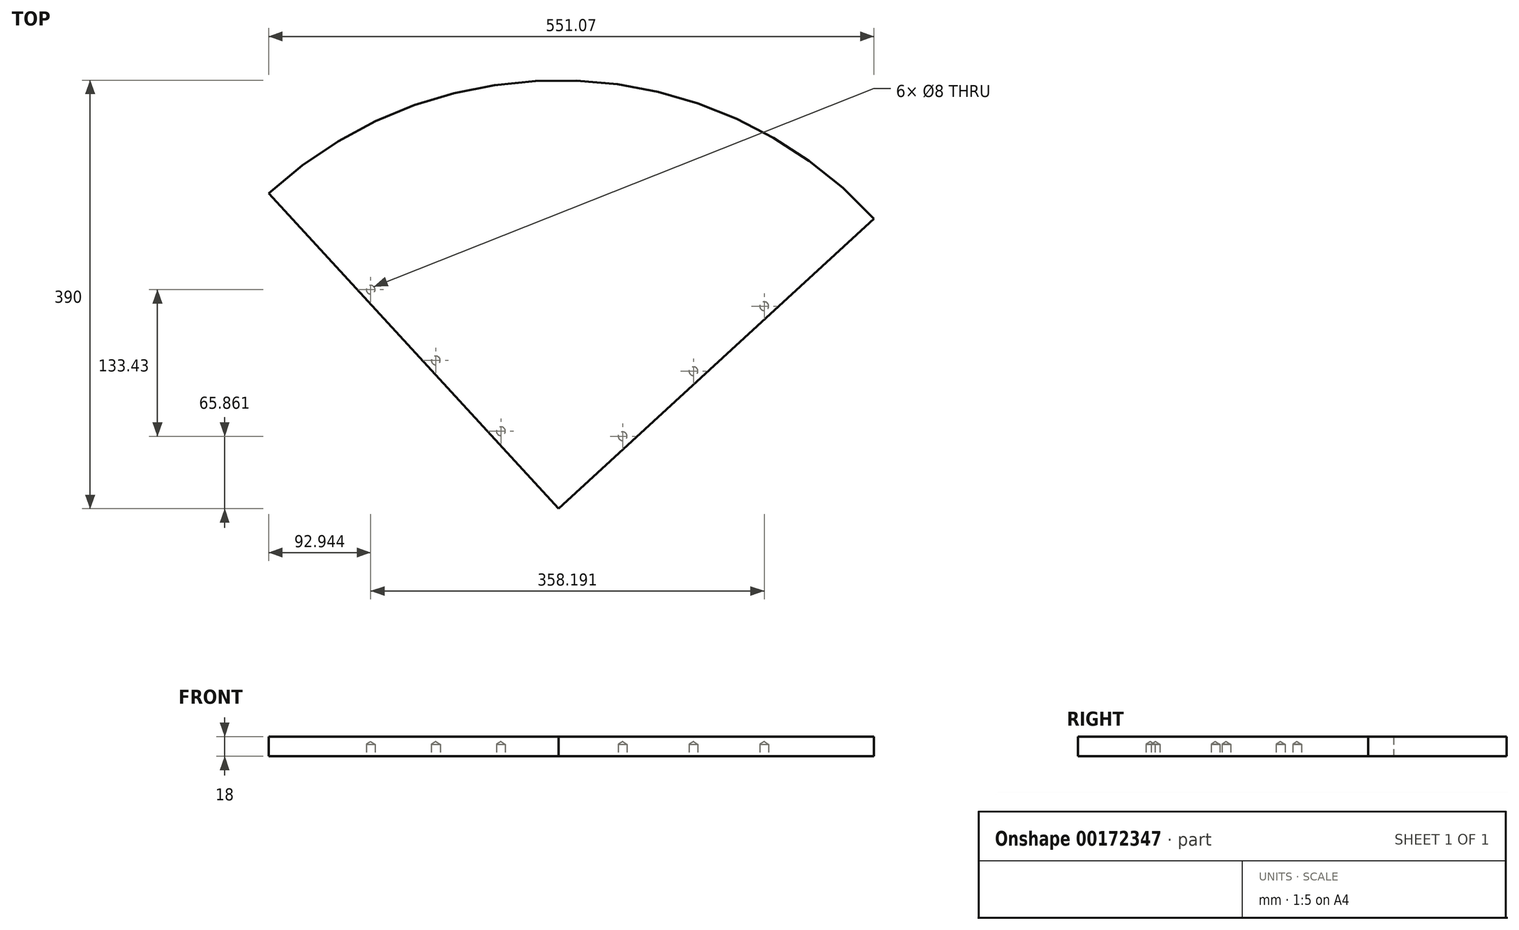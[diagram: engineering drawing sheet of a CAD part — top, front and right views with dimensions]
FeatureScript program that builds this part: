
annotation { "Feature Type Name" : "Feature", "Feature Type Description" : "" }
export const myFeature = defineFeature(function(context is Context, id is Id, definition is map)
    precondition{}
    {
        {
            var Q0;
            Q0=qCreatedBy(makeId("Top.planeOp"),FACE);
            var sketch = newSketch(context, id + "F0", { "sketchPlane" : qUnion([Q0])});
            skArc(sketch, "E0", {"start": v(-264.03, 287.04) * mm, "mid": v(16.27, 389.66) * mm, "end": v(287.04, 264.03) * mm});
            skLineSegment(sketch, "E1", {"start": v(-264.03, 287.04) * mm, "end": v(0, 0) * mm});
            skLineSegment(sketch, "E2", {"start": v(287.04, 264.03) * mm, "end": v(0, 0) * mm});
            skSolve(sketch);
        }
        {
            var Q0;
            {var subQ0=sQuery(id+"F0.wireOp",EDGE,"qqqJjdmg-fhSf-ph05-KDBg-snlAx8Mx0EB6");Q0=makeQuery(id+"F0.imprint","IMPRINT",FACE,{"disambiguationData":[TD([[makeQuery(id+"F0.imprint","IMPRINT",EDGE,{"derivedFrom":subQ0}),1.0]])]});}
            var Q1;
            {var subQ0=sQuery(id+"F0.wireOp",EDGE,"E1");Q1=makeQuery(id+"F0.imprint","IMPRINT",FACE,{"disambiguationData":[TD([[makeQuery(id+"F0.imprint","IMPRINT",EDGE,{"derivedFrom":subQ0}),1.0]])]});}
            var Q2;
            {var subQ0=sQuery(id+"F0.wireOp",EDGE,"E2");Q2=makeQuery(id+"F0.imprint","IMPRINT",FACE,{"disambiguationData":[TD([[makeQuery(id+"F0.imprint","IMPRINT",EDGE,{"derivedFrom":subQ0}),-1.0]])]});}
            extrude(context, id + "F1", {"entities" : qUnion([Q0, Q1, Q2]), "depth" : 18 * mm});
        }
        {
            var Q0;
            Q0=makeQuery(id+"F1.opExtrude","CAP_FACE",FACE,{"disambiguationData":[OSD([sQuery(id+"F0.wireOp",EDGE,"E0"),sQuery(id+"F0.wireOp",EDGE,"E1"),sQuery(id+"F0.wireOp",EDGE,"E2")])],"isStart":true});
            var sketch = newSketch(context, id + "F2", { "sketchPlane" : qUnion([Q0])});
            skPoint(sketch, "E3", {"position": v(-52.61, -70.5) * mm});
            skPoint(sketch, "E4", {"position": v(-111.85, -134.9) * mm});
            skPoint(sketch, "E5", {"position": v(-171.09, -199.3) * mm});
            skPoint(sketch, "E6", {"position": v(58.3, -65.86) * mm});
            skPoint(sketch, "E7", {"position": v(122.7, -125.1) * mm});
            skPoint(sketch, "E8", {"position": v(187.1, -184.33) * mm});
            skSolve(sketch);
        }
        {
            var Q0;
            Q0=sQuery(id+"F2.wireOp",VERTEX,"E4");
            var Q1;
            Q1=sQuery(id+"F2.wireOp",VERTEX,"E3");
            var Q2;
            Q2=sQuery(id+"F2.wireOp",VERTEX,"E6");
            var Q3;
            Q3=sQuery(id+"F2.wireOp",VERTEX,"E7");
            var Q4;
            Q4=sQuery(id+"F2.wireOp",VERTEX,"E8");
            var Q5;
            Q5=sQuery(id+"F2.wireOp",VERTEX,"E5");
            var Q6;
            Q6=makeQuery(id+"F1.opExtrude","SWEPT_BODY",BODY,{"disambiguationData":[OSD([sQuery(id+"F0.wireOp",EDGE,"E0"),sQuery(id+"F0.wireOp",EDGE,"E1"),sQuery(id+"F0.wireOp",EDGE,"E2")])]});
            hole(context, id + "F3", {"style" : HoleStyle.SIMPLE, "endStyle" : HoleEndStyle.BLIND, "holeDiameter" : 8 * mm, "holeDepth" : 11 * mm, "startFromSketch" : true, "locations" : qUnion([Q0, Q1, Q2, Q3, Q4, Q5]), "scope" : qUnion([Q6])});
        }
    });
